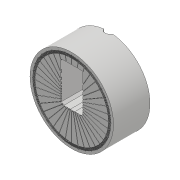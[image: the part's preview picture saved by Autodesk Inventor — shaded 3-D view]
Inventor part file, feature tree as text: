
AUTODESK INVENTOR PART (.ipt)
format: ipt  version: 2018 (Build 220112000, 112)  size: 2,378,752 bytes
history: native  units: mm
features: sketch x29, extrude x25, projected_geometry x23, fillet x9, hole x4, chamfer x3, pattern_circular x2, mirror x1
ambient origin geometry x8: Origin, YZ Plane, XZ Plane, XY Plane, X Axis, Y Axis, Z Axis, Center Point
bodies: Solid1 (feature_tree)
feature tree (96):
  extrude  "Extrusion1"  Depth=45.0mm
  extrude  "Extrusion2"  Depth=2.25mm
  hole  "Hole1"  [1 undecoded]
  hole  "Hole2"  [1 undecoded]
  fillet  "Fillet1"  Radius=14.0mm
  extrude  "Extrusion3"  Depth=18.5mm
  extrude  "Extrusion4"  Depth=10.0mm
  extrude  "Extrusion5"  Depth=2.0mm
  extrude  "Extrusion6"  Depth=2.0mm
  hole  "Hole3"  [1 undecoded]
  extrude  "Extrusion7"  Depth=0.5mm
  extrude  "Extrusion8"  Depth=5.0mm TaperAngle=0.0deg
  extrude  "Extrusion9"  Depth=10.0mm
  extrude  "Extrusion10"  Depth=10.0mm
  extrude  "Extrusion11"  Depth=14.5mm
  extrude  "Extrusion12"  Depth=20.0mm
  extrude  "Extrusion13"  Depth=5.0mm
  extrude  "Extrusion14"  Depth=2.25mm
  extrude  "Extrusion15"  Depth=5.0mm
  extrude  "Extrusion16"  Depth=5.0mm
  extrude  "Extrusion17"  Depth=1.0mm
  chamfer  "Chamfer1"  Distance=1.0mm
  fillet  "Fillet7"  Radius=20.7mm
  fillet  "Fillet8"  Radius=32.0mm
  mirror  "Mirror1"
  extrude  "Extrusion18"  Depth=1.0mm TaperAngle=0.0deg
  hole  "Hole5"  [1 undecoded]
  extrude  "Extrusion19"  Depth=0.2mm TaperAngle=0.0deg
  extrude  "Extrusion20"  Depth=0.5mm TaperAngle=0.0deg
  extrude  "Extrusion21"  Depth=5.0mm TaperAngle=0.0deg
  fillet  "Fillet9"  Radius=5.0mm
  extrude  "Extrusion22"  Depth=1.0mm TaperAngle=0.0deg
  chamfer  "Chamfer2"  Distance=2.0mm Angle=45.0deg
  chamfer  "Chamfer3"  Distance=1.5mm
  fillet  "Fillet10"  Radius=0.5mm
  extrude  "Extrusion26"  Depth=22.55mm TaperAngle=0.0deg
  fillet  "Fillet12"  Radius=5.0mm
  pattern_circular  "Circular Pattern4"  [2 undecoded]
  extrude  "Extrusion23"  Depth=1.0mm
  fillet  "Fillet11"  Radius=13.0mm
  pattern_circular  "Circular Pattern2"  [2 undecoded]
  extrude  "Extrusion27"  Depth=1.0mm
  fillet  "Fillet13"  Radius=20.0mm
  fillet  "Fillet14"  Radius=4.5mm
  sketch  "Sketch1"  dims[d0=24.5mm d1=45.0mm]
  sketch  "Sketch2"  dims[d2=1.95mm d3=0.0mm d4=2.25mm]
  projected_geometry  "Projected Loop1"
  sketch  "Sketch3"  dims[d5=20.0mm d6=2.25mm]
  projected_geometry  "Projected Loop2"
  sketch  "Sketch4"  dims[d7=5.25mm d8=5.25mm d9=14.0mm]
  projected_geometry  "Projected Loop3"
  sketch  "Sketch5"  dims[d10=5.25mm d11=18.5mm]
  projected_geometry  "Projected Loop4"
  sketch  "Sketch6"  dims[d12=10.0mm d13=0.0mm d14=20.5mm]
  projected_geometry  "Projected Loop5"
  sketch  "Sketch7"  dims[d15=2.0mm d16=2.195mm]
  projected_geometry  "Projected Loop6"
  sketch  "Sketch8"  dims[d17=2.0mm]
  projected_geometry  "Projected Loop7"
  sketch  "Sketch9"  dims[d18=2.4mm d19=6.0mm d20=4.4mm d21=2.0mm d22=90.0deg d23=8.0mm d24=20.594885mm d25=20.5mm]
  projected_geometry  "Projected Loop8"
  projected_geometry  "Projected Loop9"
  sketch  "Sketch10"  dims[d26=26.65mm d27=2.0mm]
  projected_geometry  "Projected Loop10"
  projected_geometry  "Projected Loop11"
  sketch  "Sketch11"  dims[d28=2.0mm]
  projected_geometry  "Projected Loop12"
  sketch  "Sketch12"  dims[d29=2.4mm d30=6.0mm d31=4.4mm d32=2.0mm d33=90.0deg d34=8.0mm d35=20.594885mm d36=0.5mm]
  sketch  "Sketch13"  dims[d37=18.0mm d38=5.0mm d39=0.0mm]
  sketch  "Sketch14"  dims[d41=10.0mm d42=0.0mm d43=24.5mm]
  projected_geometry  "Projected Loop13"
  sketch  "Sketch15"  dims[d44=1.15mm d45=0.0mm d46=10.0mm]
  sketch  "Sketch16"  dims[d47=21.0mm d48=14.5mm]
  projected_geometry  "Projected Loop14"
  sketch  "Sketch17"  dims[d49=20.0mm d50=14.5mm]
  projected_geometry  "Projected Loop15"
  sketch  "Sketch18"  dims[d51=24.5mm d52=5.0mm]
  projected_geometry  "Projected Loop16"
  sketch  "Sketch19"  dims[d53=5.0mm d54=2.25mm]
  projected_geometry  "Projected Loop17"
  sketch  "Sketch20"  dims[d55=2.25mm d56=5.0mm]
  projected_geometry  "Projected Loop18"
  sketch  "Sketch22"  dims[d57=5.0mm d58=9.0mm]
  sketch  "Sketch24"  dims[d59=14.75mm d60=4.0mm d61=1.0mm d62=0.0mm d63=20.7mm]
  projected_geometry  "Projected Loop21"
  sketch  "Sketch25"  dims[d64=2.4mm d65=6.0mm d66=4.4mm d67=2.0mm d68=90.0deg d69=8.0mm d70=20.594885mm d72=32.0mm]
  projected_geometry  "Projected Loop22"
  sketch  "Sketch26"  dims[d73=5.0mm d74=0.0mm d75=1.0mm d76=0.0mm]
  projected_geometry  "Projected Loop23"
  sketch  "Sketch27"  dims[d77=12.25mm d78=0.0mm d80=8.0mm]
  projected_geometry  "Projected Loop24"
  sketch  "Sketch28"  dims[d81=4.5mm d82=0.0mm d84=0.2mm d85=0.0mm]
  projected_geometry  "Projected Loop25"
  sketch  "Sketch29"  dims[d86=21.0mm d87=0.5mm d88=0.0mm]
  sketch  "Sketch33"  dims[d91=8.0mm d92=0.0mm d93=5.0mm d94=0.0mm d95=5.0mm d96=0.0mm]
  sketch  "Sketch34"  dims[d98=0.2mm d99=0.0mm d100=0.2mm d101=0.0mm d102=2.5mm d103=2.0mm d104=45.0deg d105=1.5mm d114=0.5mm d115=22.55mm d116=0.0mm d117=5.0mm d118=5.0mm d119=13.0mm d120=13.0mm d121=3.2mm d122=6.0mm d123=6.3mm d124=2.0mm d125=90.0deg d126=8.0mm d127=20.594885mm d128=19.0mm d129=0.0mm d130=95.0mm d131=20.0mm d132=0.0mm d133=4.5mm d134=4.5mm d135=4.5mm d136=4.5mm d137=2.0mm d138=0.0mm d139=0.8mm d140=10.0mm d141=36.0mm d142=3.5mm d143=0.0mm d144=5.0mm d145=2.0mm d146=45.0deg d147=3.0mm d148=2.0mm d149=45.0deg d150=3.0mm d151=0.5mm d152=90.0mm d153=1.0mm d154=0.0mm d158=0.25mm d159=190.0mm d160=180.0deg d174=0.3mm d175=3.0mm d176=43.0mm d177=0.5mm d178=0.0mm d179=0.15mm d180=3600.0mm d181=360.0deg d183=2.0mm d184=0.0mm d185=0.5mm d186=0.25mm d162=1.0mm d163=1.0mm]
note: 8 required parameter values undecoded (feature->parameter linkage not recoverable at this tier; creation-order binding heuristic only, values carry confidence <= 0.55)
